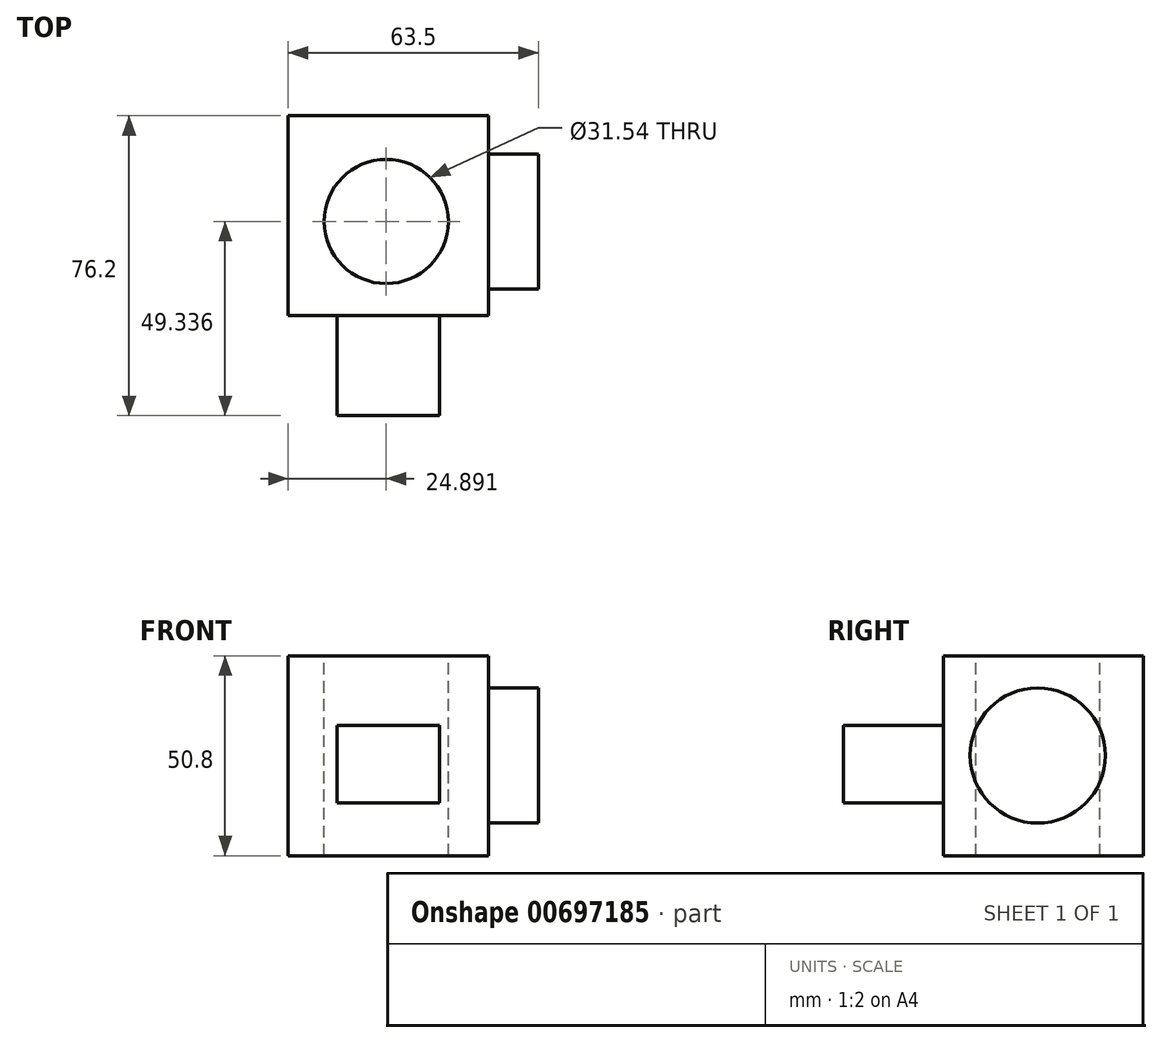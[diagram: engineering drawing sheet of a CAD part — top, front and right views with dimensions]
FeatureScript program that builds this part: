
annotation { "Feature Type Name" : "Feature", "Feature Type Description" : "" }
export const myFeature = defineFeature(function(context is Context, id is Id, definition is map)
    precondition{}
    {
        {
            var Q0;
            Q0=qCreatedBy(makeId("Front.planeOp"),FACE);
            var sketch = newSketch(context, id + "F0", { "sketchPlane" : qUnion([Q0])});
            skLineSegment(sketch, "E0", {"start": v(-53.15, 50.8) * mm, "end": v(-53.15, 0) * mm});
            skLineSegment(sketch, "E1", {"start": v(-53.15, 0) * mm, "end": v(-2.35, 0) * mm});
            skLineSegment(sketch, "E2", {"start": v(-2.35, 0) * mm, "end": v(-2.35, 50.8) * mm});
            skLineSegment(sketch, "E3", {"start": v(-2.35, 50.8) * mm, "end": v(-53.15, 50.8) * mm});
            skSolve(sketch);
        }
        {
            var Q0;
            Q0 = qSketchRegion(id + "F0", true);
            extrude(context, id + "F1", {"entities" : qUnion([Q0]), "depth" : 50.8 * mm, "offsetDistance" : 25.4 * mm});
        }
        {
            var Q0;
            Q0=makeQuery(id+"F1.opExtrude","CAP_FACE",FACE,{"disambiguationData":[OSD([sQuery(id+"F0.wireOp",EDGE,"E0"),sQuery(id+"F0.wireOp",EDGE,"E1"),sQuery(id+"F0.wireOp",EDGE,"E2"),sQuery(id+"F0.wireOp",EDGE,"E3")])],"isStart":false});
            var sketch = newSketch(context, id + "F2", { "sketchPlane" : qUnion([Q0])});
            skLineSegment(sketch, "E4.bottom", {"start": v(-40.82, 33.14) * mm, "end": v(-14.77, 33.14) * mm});
            skLineSegment(sketch, "E4.top", {"start": v(-40.82, 13.37) * mm, "end": v(-14.77, 13.37) * mm});
            skLineSegment(sketch, "E4.left", {"start": v(-40.82, 33.14) * mm, "end": v(-40.82, 13.37) * mm});
            skLineSegment(sketch, "E4.right", {"start": v(-14.77, 33.14) * mm, "end": v(-14.77, 13.37) * mm});
            skSolve(sketch);
        }
        {
            var Q0;
            Q0=makeQuery(id+"F2.imprint","IMPRINT",FACE,{"disambiguationData":[TD([[makeQuery(id+"F2.imprint","IMPRINT",EDGE,{"derivedFrom":sQuery(id+"F2.wireOp",EDGE,"E4.bottom")}),-1.0]])]});
            extrude(context, id + "F3", {"entities" : qUnion([Q0]), "operationType" : NewBodyOperationType.ADD, "depth" : 25.4 * mm, "offsetDistance" : 25.4 * mm});
        }
        {
            var Q0;
            Q0=makeQuery(id+"F1.opExtrude","SWEPT_FACE",FACE,{"disambiguationData":[OSD([sQuery(id+"F0.wireOp",EDGE,"E3")])]});
            var sketch = newSketch(context, id + "F4", { "sketchPlane" : qUnion([Q0])});
            skCircle(sketch, "E5", {"center": v(-28.26, -26.86) * mm, "radius": 15.77 * mm});
            skSolve(sketch);
        }
        {
            var Q0;
            Q0=makeQuery(id+"F4.imprint","IMPRINT",FACE,{"disambiguationData":[TD([[makeQuery(id+"F4.imprint","IMPRINT",EDGE,{"derivedFrom":sQuery(id+"F4.wireOp",EDGE,"E5")}),1.0]])]});
            extrude(context, id + "F5", {"entities" : qUnion([Q0]), "operationType" : NewBodyOperationType.REMOVE, "oppositeDirection" : true, "depth" : 50.8 * mm, "offsetDistance" : 25.4 * mm});
        }
        {
            var Q0;
            Q0=makeQuery(id+"F1.opExtrude","SWEPT_FACE",FACE,{"disambiguationData":[OSD([sQuery(id+"F0.wireOp",EDGE,"E2")])]});
            var sketch = newSketch(context, id + "F6", { "sketchPlane" : qUnion([Q0])});
            skCircle(sketch, "E6", {"center": v(-26.86, 25.47) * mm, "radius": 17.17 * mm});
            skSolve(sketch);
        }
        {
            var Q0;
            Q0=makeQuery(id+"F6.imprint","IMPRINT",FACE,{"disambiguationData":[TD([[makeQuery(id+"F6.imprint","IMPRINT",EDGE,{"derivedFrom":sQuery(id+"F6.wireOp",EDGE,"E6")}),1.0]])]});
            extrude(context, id + "F7", {"entities" : qUnion([Q0]), "operationType" : NewBodyOperationType.ADD, "depth" : 12.7 * mm, "offsetDistance" : 25.4 * mm});
        }
    });
